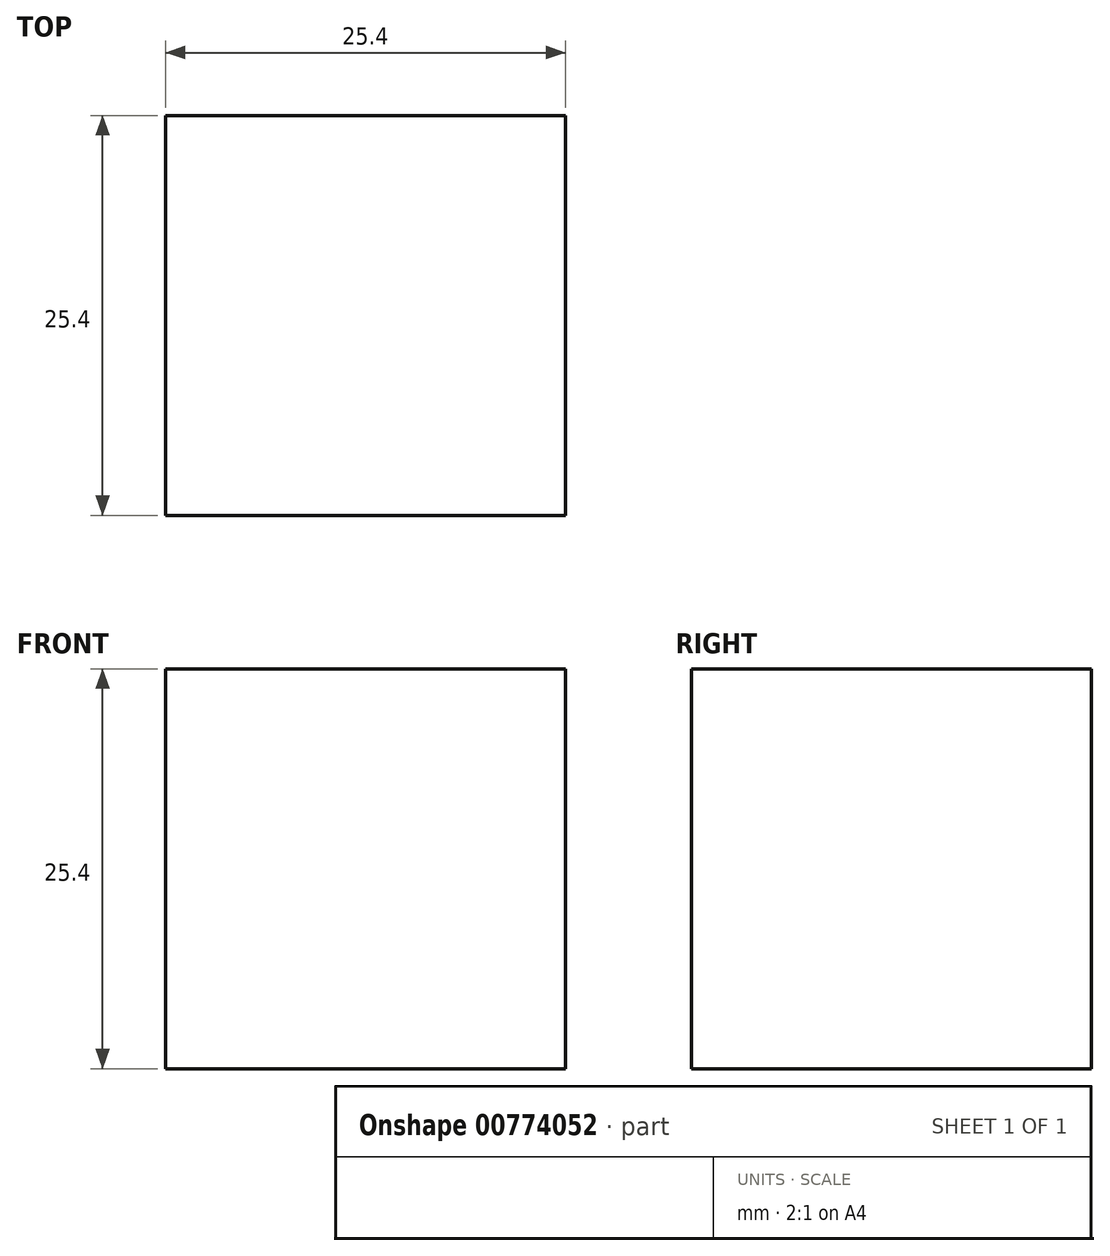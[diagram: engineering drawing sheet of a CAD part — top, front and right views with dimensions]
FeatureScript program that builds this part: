
annotation { "Feature Type Name" : "Feature", "Feature Type Description" : "" }
export const myFeature = defineFeature(function(context is Context, id is Id, definition is map)
    precondition{}
    {
        {
            var Q0;
            Q0=qCreatedBy(makeId("Top.planeOp"),FACE);
            var sketch = newSketch(context, id + "F0", { "sketchPlane" : qUnion([Q0])});
            skLineSegment(sketch, "E0.bottom", {"start": v(12.7, 12.7) * mm, "end": v(-12.7, 12.7) * mm});
            skLineSegment(sketch, "E0.top", {"start": v(12.7, -12.7) * mm, "end": v(-12.7, -12.7) * mm});
            skLineSegment(sketch, "E0.left", {"start": v(12.7, 12.7) * mm, "end": v(12.7, -12.7) * mm});
            skLineSegment(sketch, "E0.right", {"start": v(-12.7, 12.7) * mm, "end": v(-12.7, -12.7) * mm});
            skPoint(sketch, "E0.middle", {"position": v(0, 0) * mm});
            skSolve(sketch);
        }
        {
            var Q0;
            Q0=makeQuery(id+"F0.imprint","IMPRINT",FACE,{"disambiguationData":[TD([[makeQuery(id+"F0.imprint","IMPRINT",EDGE,{"derivedFrom":sQuery(id+"F0.wireOp",EDGE,"E0.bottom")}),1.0]])]});
            extrude(context, id + "F1", {"entities" : qUnion([Q0]), "depth" : 25.4 * mm, "offsetDistance" : 25.4 * mm});
        }
    });
